# Revit family: Drain_Floor-Jay R.Smith-Rectangle-Type-3320-3321_Series
name_source: partatom
category: Plumbing Fixtures
units: mm (PartAtom-declared; Revit-internal decimal feet)

## family parameters
Always vertical = No
Cut with Voids When Loaded = No
OmniClass Number = 23.70.50.21.24
OmniClass Title = Waste Water Drains
Part Type = Normal
Room Calculation Point = No
Round Connector Dimension = Use Diameter
Shared = Yes
Work Plane-Based = Yes

## types (12) — shared parameters
Assembly Code = D2030300
C - flashing clamp = No
CI- All Duco Cast Iron Receptor and Grate = No
CW Connection = No
Default Elevation = 0"
Description = Sani-Ceptor® Sanitary Acid Resistant Coated Sanitary Floor and Indirect Waste Drains with Deep Receptor and Rectangular Nickel Bronze Top
FBS - Aluminum Flat Bottom Strainer = No
Finish = Metal-Jay R. Smith-Cast Iron
G-All Galvanized Receptor and Grate = No
HW Connection = No
Height = 10 3/4"
Installation Type = Floor Mounted
Length = 14"
Manufacturer = Jay R. Smith
Material = Metal-Jay R. Smith-Cast Iron
PDBS - Polished Aluminum Dome Bottom Strainer = No
Product Documentation Link = https://www.jrsmith.com
Product Page URL = https://www.jrsmith.com
Stainless Steel Receptor = No
U - Vandal Proof Screw = No
URL = http://www.jrsmith.com
Vent Connection = No
Waste Connection = Yes
Width = 8"

## per-type parameters (varying)
| type | Connection Radius | Connection Size | Outlet Connection Description | Type Comments |
| 3320Y02 | 1" | 2" | 2" No-HUB Outlet Connection | With dome bottom strainer |
| 3320C03 | 1 1/2" | 3" | 3" Caulk Outlet Connection | With dome bottom strainer |
| 3320C02 | 1" | 2" | 2" Caulk Outlet Connection | With dome bottom strainer |
| 3320Y03 | 1 1/2" | 3" | 3" No-HUB Outlet Connection | With dome bottom strainer |
| 3321Y02 | 1" | 2" | 2" No-HUB Outlet Connection | With sediment bucket |
| 3321C03 | 1 1/2" | 3" | 3" Caulk Outlet Connection | With sediment bucket |
| 3321C02 | 1" | 2" | 2" Caulk Outlet Connection | With sediment bucket |
| 3321Y03 | 1 1/2" | 3" | 3" No-HUB Outlet Connection | With sediment bucket |
| 3320C04 | 2" | 4" | 4" Caulk Outlet Connection | With dome bottom strainer |
| 3320Y04 | 2" | 4" | 4" No-HUB Outlet Connection | With dome bottom strainer |
| 3321C04 | 2" | 4" | 4" Caulk Outlet Connection | With sediment bucket |
| 3321Y04 | 2" | 4" | 4" No-HUB Outlet Connection | With sediment bucket |

note: column(s) folded — value = type name in every type: Model

## geometry (parser evidence)
native form markers: Sweep x2
no freeform markers — native parametric forms only
